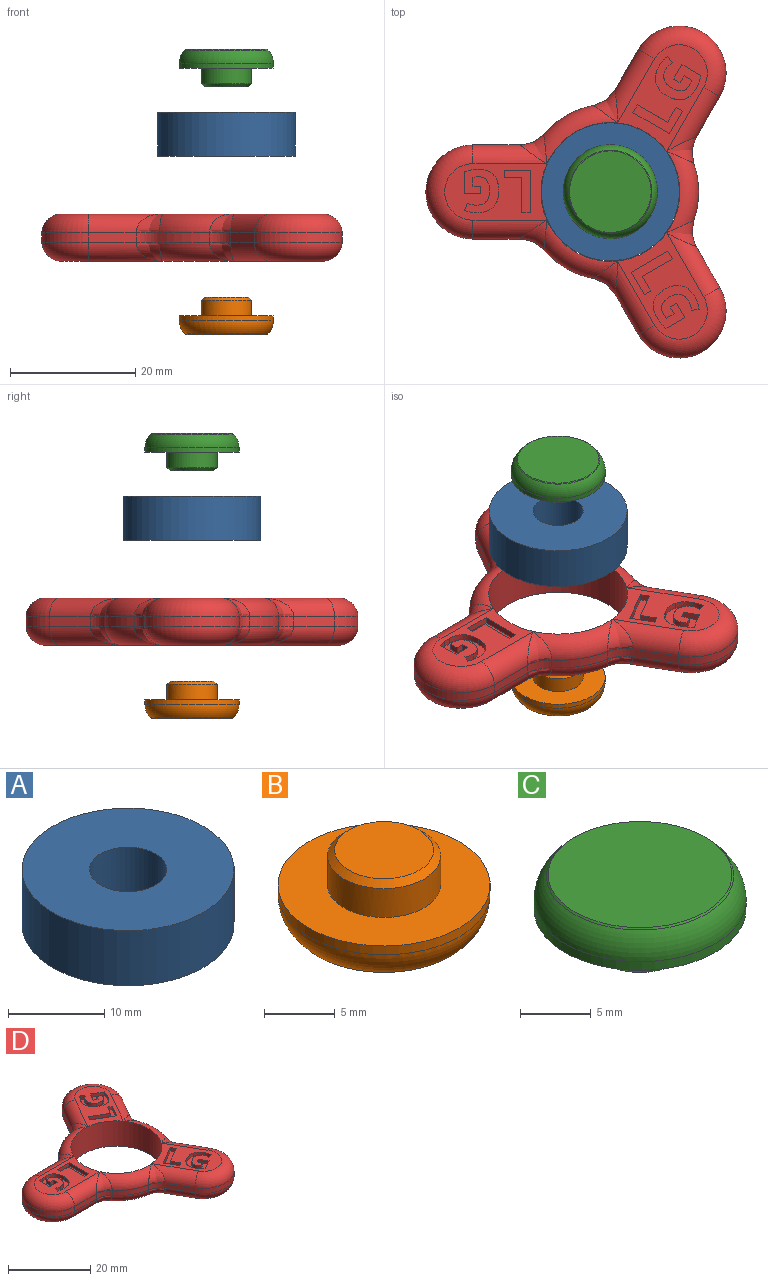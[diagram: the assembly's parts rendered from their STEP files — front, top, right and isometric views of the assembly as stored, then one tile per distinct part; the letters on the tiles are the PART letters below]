
ASSEMBLY  parts=4 mates=3
PART A: 4 faces, bbox 22x22x7 mm
  f0: cylinder r=4mm len=8mm, axis (0,0,-1), area 175.9mm2, adj f2,f3
  f1: cylinder r=11mm len=22mm, axis (0,0,-1), area 483.8mm2, adj f2,f3
  f2: plane 22x22mm, normal (0,0,1), area 329.9mm2, adj f0,f1
  f3: plane 22x22mm, normal (0,0,-1), area 329.9mm2, adj f0,f1
PART B: 8 faces, bbox 16.2x16.2x6.8 mm
  f0: cylinder r=4mm len=8mm, axis (0,0,-1), area 62.8mm2, adj f4,f7
  f1: plane 7x7mm, normal (0,0,1), area 38.5mm2, adj f7
  f2: cylinder r=7.5mm len=15mm, axis (0,0,1), area 35.7mm2, adj f4,f6
  f3: plane 13x13mm, normal (0,0,-1), area 132.7mm2, adj f5
  f4: plane 15x15mm, normal (0,0,1), area 126.4mm2, adj f0,f2
  f5: cone r=6.5mm half-angle=45deg, axis (0,0,1), area 7.1mm2, adj f3,f6
  f6: torus R=4.5mm, axis (0,0,-1), area 106.6mm2, adj f2,f5
  f7: cone r=3.5mm half-angle=45deg, axis (0,0,-1), area 16.7mm2, adj f0,f1
PART C: 8 faces, bbox 16.2x16.2x6.8 mm
  f0: cylinder r=4mm len=8mm, axis (0,0,1), area 62.8mm2, adj f4,f7
  f1: plane 7x7mm, normal (0,0,-1), area 38.5mm2, adj f7
  f2: cylinder r=7.5mm len=15mm, axis (0,0,-1), area 35.7mm2, adj f4,f6
  f3: plane 13x13mm, normal (0,0,1), area 132.7mm2, adj f5
  f4: plane 15x15mm, normal (0,0,-1), area 126.4mm2, adj f0,f2
  f5: cone r=6.5mm half-angle=45deg, axis (0,0,-1), area 7.1mm2, adj f3,f6
  f6: torus R=4.5mm, axis (0,0,1), area 106.6mm2, adj f2,f5
  f7: cone r=4mm half-angle=45deg, axis (0,0,1), area 16.7mm2, adj f0,f1
PART D: 223 faces, bbox 49.1x54.2x7.5 mm
  f0: plane 16.96x14.29mm, normal (0,0,1), area 97.3mm2, adj f9,f39,f41,f42,f196,f197,f198,f199
  f1: plane 16.96x14.29mm, normal (0,0,1), area 97.3mm2, adj f9,f31,f33,f35,f169,f170,f171,f172
  f2: plane 16.29x9mm, normal (0,0,1), area 97.3mm2, adj f9,f34,f36,f38,f142,f143,f144,f145
  f3: plane 16.96x14.29mm, normal (0,0,-1), area 97.3mm2, adj f9,f27,f29,f30,f115,f116,f117,f118
  f4: plane 16.96x14.29mm, normal (0,0,-1), area 97.3mm2, adj f9,f19,f21,f23,f88,f89,f90,f91
  f5: plane 16.29x9mm, normal (0,0,-1), area 97.3mm2, adj f9,f22,f24,f26,f61,f62,f63,f64
  f6: cylinder r=14.08mm len=9.19mm, axis (0,0,-1), area 14mm2, adj f25,f37,f47,f56
  f7: cylinder r=14.08mm len=7.96mm, axis (0,0,-1), area 14mm2, adj f20,f32,f44,f53
  f8: cylinder r=14.08mm len=7.96mm, axis (0,0,-1), area 14mm2, adj f28,f40,f50,f59
  f9: cylinder r=11.07mm len=22.15mm, axis (0,0,-1), area 521.9mm2, adj f0,f1,f2,f3,f4,f5,f20,f25
  f10: plane 7.5x1.5mm, normal (0,-1,0), area 11.3mm2, adj f12,f22,f34,f53
  f11: plane 7.5x1.5mm, normal (0,1,0), area 11.3mm2, adj f12,f26,f38,f50
  f12: cylinder r=7.5mm len=15mm, axis (0,0,-1), area 35.3mm2, adj f10,f11,f24,f36
  f13: plane 6.5x3.75mm, normal (0.87,0.5,0), area 11.3mm2, adj f15,f23,f35,f56
  f14: plane 6.5x3.75mm, normal (-0.87,-0.5,0), area 11.3mm2, adj f15,f19,f31,f44
  f15: cylinder r=7.5mm len=14mm, axis (0,0,-1), area 35.3mm2, adj f13,f14,f21,f33
  f16: plane 6.5x3.75mm, normal (-0.87,0.5,0), area 11.3mm2, adj f18,f30,f42,f59
  f17: plane 6.5x3.75mm, normal (0.87,-0.5,0), area 11.3mm2, adj f18,f27,f39,f47
  f18: cylinder r=7.5mm len=14mm, axis (0,0,-1), area 35.3mm2, adj f16,f17,f29,f41
  f19: cylinder r=3mm len=11.71mm, axis (0.5,-0.87,0), area 42.2mm2, adj f4,f14,f21,f43
  f20: torus R=11.07mm, axis (0,0,1), area 51mm2, adj f7,f9,f43,f52
  f21: torus R=4.5mm, axis (0,0,1), area 94.9mm2, adj f4,f15,f19,f23
  f22: cylinder r=3mm len=11.79mm, axis (1,0,0), area 42.2mm2, adj f5,f10,f24,f52
  f23: cylinder r=3mm len=11.71mm, axis (-0.5,0.87,0), area 42.2mm2, adj f4,f13,f21,f55
  f24: torus R=4.5mm, axis (0,0,1), area 94.9mm2, adj f5,f12,f22,f26
  f25: torus R=11.07mm, axis (0,0,1), area 51mm2, adj f6,f9,f46,f55
  f26: cylinder r=3mm len=11.79mm, axis (-1,0,0), area 42.2mm2, adj f5,f11,f24,f49
  f27: cylinder r=3mm len=11.71mm, axis (0.5,0.87,0), area 42.2mm2, adj f3,f17,f29,f46
  f28: torus R=11.07mm, axis (0,0,1), area 51mm2, adj f8,f9,f49,f58
  f29: torus R=4.5mm, axis (0,0,1), area 94.9mm2, adj f3,f18,f27,f30
  f30: cylinder r=3mm len=11.71mm, axis (-0.5,-0.87,0), area 42.2mm2, adj f3,f16,f29,f58
  f31: cylinder r=3mm len=11.71mm, axis (-0.5,0.87,0), area 42.2mm2, adj f1,f14,f33,f45
  f32: torus R=11.07mm, axis (0,0,1), area 51mm2, adj f7,f9,f45,f54
  f33: torus R=4.5mm, axis (0,0,1), area 94.9mm2, adj f1,f15,f31,f35
  f34: cylinder r=3mm len=11.79mm, axis (-1,0,0), area 42.2mm2, adj f2,f10,f36,f54
  f35: cylinder r=3mm len=11.71mm, axis (0.5,-0.87,0), area 42.2mm2, adj f1,f13,f33,f57
  f36: torus R=4.5mm, axis (0,0,1), area 94.9mm2, adj f2,f12,f34,f38
  f37: torus R=11.07mm, axis (0,0,1), area 51mm2, adj f6,f9,f48,f57
  f38: cylinder r=3mm len=11.79mm, axis (1,0,0), area 42.2mm2, adj f2,f11,f36,f51
  f39: cylinder r=3mm len=11.71mm, axis (-0.5,-0.87,0), area 42.2mm2, adj f0,f17,f41,f48
  f40: torus R=11.07mm, axis (0,0,1), area 51mm2, adj f8,f9,f51,f60
  f41: torus R=4.5mm, axis (0,0,1), area 94.9mm2, adj f0,f18,f39,f42
  f42: cylinder r=3mm len=11.71mm, axis (0.5,0.87,0), area 42.2mm2, adj f0,f16,f41,f60
  f43: bspline ~5.22x3.84mm, area 14.7mm2, adj f19,f20,f44
  f44: cylinder r=5mm len=3.38mm, axis (0,0,-1), area 6.4mm2, adj f7,f14,f43,f45
  f45: bspline ~5.22x3.84mm, area 14.7mm2, adj f31,f32,f44
  f46: bspline ~4.75x4.14mm, area 14.7mm2, adj f25,f27,f47
  f47: cylinder r=5mm len=4.13mm, axis (0,0,-1), area 6.4mm2, adj f6,f17,f46,f48
  f48: bspline ~4.75x4.14mm, area 14.7mm2, adj f37,f39,f47
  f49: bspline ~4.73x4.29mm, area 14.7mm2, adj f26,f28,f50
  f50: cylinder r=5mm len=3.78mm, axis (0,0,-1), area 6.4mm2, adj f8,f11,f49,f51
  f51: bspline ~4.73x4.29mm, area 14.7mm2, adj f38,f40,f50
  f52: bspline ~4.73x4.29mm, area 14.7mm2, adj f20,f22,f53
  f53: cylinder r=5mm len=3.78mm, axis (0,0,-1), area 6.4mm2, adj f7,f10,f52,f54
  f54: bspline ~4.73x4.29mm, area 14.7mm2, adj f32,f34,f53
  f55: bspline ~4.75x4.14mm, area 14.7mm2, adj f23,f25,f56
  f56: cylinder r=5mm len=4.13mm, axis (0,0,-1), area 6.4mm2, adj f6,f13,f55,f57
  f57: bspline ~4.75x4.14mm, area 14.7mm2, adj f35,f37,f56
  f58: bspline ~5.22x3.84mm, area 14.7mm2, adj f28,f30,f59
  f59: cylinder r=5mm len=3.38mm, axis (0,0,-1), area 6.4mm2, adj f8,f16,f58,f60
  f60: bspline ~5.22x3.84mm, area 14.7mm2, adj f40,f42,f59
  f61: plane 4.15x1mm, normal (0,1,0), area 4.2mm2, adj f5,f62,f66,f67
  f62: plane 1.18x1mm, normal (1,0,0), area 1.2mm2, adj f5,f61,f63,f67
  f63: plane 2.73x1mm, normal (0,-1,0), area 2.7mm2, adj f5,f62,f64,f67
  f64: plane 5.55x1mm, normal (1,0,0), area 5.5mm2, adj f5,f63,f65,f67
  f65: plane 1.43x1mm, normal (0,-1,0), area 1.4mm2, adj f5,f64,f66,f67
  f66: plane 6.73x1mm, normal (-1,0,0), area 6.7mm2, adj f5,f61,f65,f67
  f67: plane 6.73x4.15mm, normal (0,0,-1), area 12.8mm2, adj f61,f62,f63,f64,f65,f66
  f68: plane 1.19x1mm, normal (-1,0,0), area 1.2mm2, adj f5,f69,f86,f87
  f69: plane 1.27x1mm, normal (0,1,0), area 1.3mm2, adj f5,f68,f70,f87
  f70: plane 1.4x1mm, normal (-1,0,0), area 1.4mm2, adj f5,f69,f71,f87
  f71: extruded ~1x0.91mm, area 0.9mm2, adj f5,f70,f72,f87
  f72: extruded ~1.3x1mm, area 1.5mm2, adj f5,f71,f73,f87
  f73: extruded ~1.67x1mm, area 1.8mm2, adj f5,f72,f74,f87
  f74: extruded ~1.67x1mm, area 1.8mm2, adj f5,f73,f75,f87
  f75: extruded ~1.48x1mm, area 1.7mm2, adj f5,f74,f76,f87
  f76: extruded ~1.53x1mm, area 1.6mm2, adj f5,f75,f77,f87
  f77: plane 1.14x1mm, normal (0.92,0.38,0), area 1.2mm2, adj f5,f76,f78,f87
  f78: extruded ~2x1mm, area 2.1mm2, adj f5,f77,f79,f87
  f79: extruded ~2.58x1mm, area 2.8mm2, adj f5,f78,f80,f87
  f80: extruded ~2.54x1mm, area 2.8mm2, adj f5,f79,f81,f87
  f81: extruded ~2.57x1mm, area 2.8mm2, adj f5,f80,f82,f87
  f82: extruded ~2.32x1mm, area 2.6mm2, adj f5,f81,f83,f87
  f83: extruded ~1.17x1mm, area 1.2mm2, adj f5,f82,f84,f87
  f84: extruded ~1.22x1mm, area 1.3mm2, adj f5,f83,f85,f87
  f85: plane 3.49x1mm, normal (1,0,0), area 3.5mm2, adj f5,f84,f86,f87
  f86: plane 2.67x1mm, normal (0,-1,0), area 2.7mm2, adj f5,f68,f85,f87
  f87: plane 6.91x5.52mm, normal (0,0,-1), area 22mm2, adj f68,f69,f70,f71,f72,f73,f74,f75
  f88: plane 3.6x2.08mm, normal (-0.87,-0.5,0), area 4.2mm2, adj f4,f89,f93,f94
  f89: plane 1.02x1mm, normal (-0.5,0.87,0), area 1.2mm2, adj f4,f88,f90,f94
  f90: plane 2.36x1.36mm, normal (0.87,0.5,0), area 2.7mm2, adj f4,f89,f91,f94
  f91: plane 4.8x2.77mm, normal (-0.5,0.87,0), area 5.5mm2, adj f4,f90,f92,f94
  f92: plane 1.24x1mm, normal (0.87,0.5,0), area 1.4mm2, adj f4,f91,f93,f94
  f93: plane 5.82x3.36mm, normal (0.5,-0.87,0), area 6.7mm2, adj f4,f88,f92,f94
  f94: plane 7.9x4.6mm, normal (0,0,-1), area 12.8mm2, adj f88,f89,f90,f91,f92,f93
  f95: plane 1.03x1mm, normal (0.5,-0.87,0), area 1.2mm2, adj f4,f96,f113,f114
  f96: plane 1.1x1mm, normal (-0.87,-0.5,0), area 1.3mm2, adj f4,f95,f97,f114
  f97: plane 1.21x1mm, normal (0.5,-0.87,0), area 1.4mm2, adj f4,f96,f98,f114
  f98: extruded ~1x0.83mm, area 0.9mm2, adj f4,f97,f99,f114
  f99: extruded ~1.15x1mm, area 1.5mm2, adj f4,f98,f100,f114
  f100: extruded ~1.67x1mm, area 1.8mm2, adj f4,f99,f101,f114
  f101: extruded ~1.32x1.17mm, area 1.8mm2, adj f4,f100,f102,f114
  f102: extruded ~1.59x1mm, area 1.7mm2, adj f4,f101,f103,f114
  f103: extruded ~1.14x1.08mm, area 1.6mm2, adj f4,f102,f104,f114
  f104: plane 1x0.98mm, normal (-0.79,0.61,0), area 1.2mm2, adj f4,f103,f105,f114
  f105: extruded ~1.52x1.36mm, area 2.1mm2, adj f4,f104,f106,f114
  f106: extruded ~2.69x1mm, area 2.8mm2, adj f4,f105,f107,f114
  f107: extruded ~2.08x1.73mm, area 2.8mm2, adj f4,f106,f108,f114
  f108: extruded ~2.63x1mm, area 2.8mm2, adj f4,f107,f109,f114
  f109: extruded ~1.94x1.57mm, area 2.6mm2, adj f4,f108,f110,f114
  f110: extruded ~1.06x1mm, area 1.2mm2, adj f4,f109,f111,f114
  f111: extruded ~1.21x1mm, area 1.3mm2, adj f4,f110,f112,f114
  f112: plane 3.02x1.74mm, normal (-0.5,0.87,0), area 3.5mm2, adj f4,f111,f113,f114
  f113: plane 2.31x1.33mm, normal (0.87,0.5,0), area 2.7mm2, adj f4,f95,f112,f114
  f114: plane 7.36x7.04mm, normal (0,0,-1), area 22mm2, adj f95,f96,f97,f98,f99,f100,f101,f102
  f115: plane 1.03x1mm, normal (0.5,0.87,0), area 1.2mm2, adj f3,f116,f133,f134
  f116: plane 1.1x1mm, normal (0.87,-0.5,0), area 1.3mm2, adj f3,f115,f117,f134
  f117: plane 1.21x1mm, normal (0.5,0.87,0), area 1.4mm2, adj f3,f116,f118,f134
  f118: extruded ~1x0.74mm, area 0.9mm2, adj f3,f117,f119,f134
  f119: extruded ~1.42x1mm, area 1.5mm2, adj f3,f118,f120,f134
  f120: extruded ~1.22x1.22mm, area 1.8mm2, adj f3,f119,f121,f134
  f121: extruded ~1.72x1mm, area 1.8mm2, adj f3,f120,f122,f134
  f122: extruded ~1.28x1mm, area 1.7mm2, adj f3,f121,f123,f134
  f123: extruded ~1.51x1mm, area 1.6mm2, adj f3,f122,f124,f134
  f124: plane 1.23x1mm, normal (-0.13,-0.99,0), area 1.2mm2, adj f3,f123,f125,f134
  f125: extruded ~1.94x1mm, area 2.1mm2, adj f3,f124,f126,f134
  f126: extruded ~2.08x1.78mm, area 2.8mm2, adj f3,f125,f127,f134
  f127: extruded ~2.66x1mm, area 2.8mm2, adj f3,f126,f128,f134
  f128: extruded ~1.98x1.82mm, area 2.8mm2, adj f3,f127,f129,f134
  f129: extruded ~2.46x1mm, area 2.6mm2, adj f3,f128,f130,f134
  f130: extruded ~1x0.97mm, area 1.2mm2, adj f3,f129,f131,f134
  f131: extruded ~1x0.91mm, area 1.3mm2, adj f3,f130,f132,f134
  f132: plane 3.02x1.74mm, normal (-0.5,-0.87,0), area 3.5mm2, adj f3,f131,f133,f134
  f133: plane 2.31x1.33mm, normal (-0.87,0.5,0), area 2.7mm2, adj f3,f115,f132,f134
  f134: plane 7.43x7mm, normal (0,0,-1), area 22mm2, adj f115,f116,f117,f118,f119,f120,f121,f122
  f135: plane 3.6x2.08mm, normal (0.87,-0.5,0), area 4.2mm2, adj f3,f136,f140,f141
  f136: plane 1.02x1mm, normal (-0.5,-0.87,0), area 1.2mm2, adj f3,f135,f137,f141
  f137: plane 2.36x1.36mm, normal (-0.87,0.5,0), area 2.7mm2, adj f3,f136,f138,f141
  f138: plane 4.8x2.77mm, normal (-0.5,-0.87,0), area 5.5mm2, adj f3,f137,f139,f141
  f139: plane 1.24x1mm, normal (-0.87,0.5,0), area 1.4mm2, adj f3,f138,f140,f141
  f140: plane 5.82x3.36mm, normal (0.5,0.87,0), area 6.7mm2, adj f3,f135,f139,f141
  f141: plane 6.96x6.54mm, normal (0,0,-1), area 12.8mm2, adj f135,f136,f137,f138,f139,f140
  f142: plane 4.15x1mm, normal (0,-1,0), area 4.2mm2, adj f2,f143,f147,f148
  f143: plane 1.18x1mm, normal (1,0,0), area 1.2mm2, adj f2,f142,f144,f148
  f144: plane 2.73x1mm, normal (0,1,0), area 2.7mm2, adj f2,f143,f145,f148
  f145: plane 5.55x1mm, normal (1,0,0), area 5.5mm2, adj f2,f144,f146,f148
  f146: plane 1.43x1mm, normal (0,1,0), area 1.4mm2, adj f2,f145,f147,f148
  f147: plane 6.73x1mm, normal (-1,0,0), area 6.7mm2, adj f2,f142,f146,f148
  f148: plane 6.73x4.15mm, normal (0,0,1), area 12.8mm2, adj f142,f143,f144,f145,f146,f147
  f149: plane 1.19x1mm, normal (-1,0,0), area 1.2mm2, adj f2,f150,f167,f168
  f150: plane 1.27x1mm, normal (0,-1,0), area 1.3mm2, adj f2,f149,f151,f168
  f151: plane 1.4x1mm, normal (-1,0,0), area 1.4mm2, adj f2,f150,f152,f168
  f152: extruded ~1x0.91mm, area 0.9mm2, adj f2,f151,f153,f168
  f153: extruded ~1.3x1mm, area 1.5mm2, adj f2,f152,f154,f168
  f154: extruded ~1.67x1mm, area 1.8mm2, adj f2,f153,f155,f168
  f155: extruded ~1.67x1mm, area 1.8mm2, adj f2,f154,f156,f168
  f156: extruded ~1.48x1mm, area 1.7mm2, adj f2,f155,f157,f168
  f157: extruded ~1.53x1mm, area 1.6mm2, adj f2,f156,f158,f168
  f158: plane 1.14x1mm, normal (0.92,-0.38,0), area 1.2mm2, adj f2,f157,f159,f168
  f159: extruded ~2x1mm, area 2.1mm2, adj f2,f158,f160,f168
  f160: extruded ~2.58x1mm, area 2.8mm2, adj f2,f159,f161,f168
  f161: extruded ~2.54x1mm, area 2.8mm2, adj f2,f160,f162,f168
  f162: extruded ~2.57x1mm, area 2.8mm2, adj f2,f161,f163,f168
  f163: extruded ~2.32x1mm, area 2.6mm2, adj f2,f162,f164,f168
  f164: extruded ~1.17x1mm, area 1.2mm2, adj f2,f163,f165,f168
  f165: extruded ~1.22x1mm, area 1.3mm2, adj f2,f164,f166,f168
  f166: plane 3.49x1mm, normal (1,0,0), area 3.5mm2, adj f2,f165,f167,f168
  f167: plane 2.67x1mm, normal (0,1,0), area 2.7mm2, adj f2,f149,f166,f168
  f168: plane 6.91x5.52mm, normal (0,0,1), area 22mm2, adj f149,f150,f151,f152,f153,f154,f155,f156
  f169: plane 1.03x1mm, normal (0.5,-0.87,0), area 1.2mm2, adj f1,f170,f187,f188
  f170: plane 1.1x1mm, normal (0.87,0.5,0), area 1.3mm2, adj f1,f169,f171,f188
  f171: plane 1.21x1mm, normal (0.5,-0.87,0), area 1.4mm2, adj f1,f170,f172,f188
  f172: extruded ~1x0.74mm, area 0.9mm2, adj f1,f171,f173,f188
  f173: extruded ~1.42x1mm, area 1.5mm2, adj f1,f172,f174,f188
  f174: extruded ~1.22x1.22mm, area 1.8mm2, adj f1,f173,f175,f188
  f175: extruded ~1.72x1mm, area 1.8mm2, adj f1,f174,f176,f188
  f176: extruded ~1.28x1mm, area 1.7mm2, adj f1,f175,f177,f188
  f177: extruded ~1.51x1mm, area 1.6mm2, adj f1,f176,f178,f188
  f178: plane 1.23x1mm, normal (-0.13,0.99,0), area 1.2mm2, adj f1,f177,f179,f188
  f179: extruded ~1.94x1mm, area 2.1mm2, adj f1,f178,f180,f188
  f180: extruded ~2.08x1.78mm, area 2.8mm2, adj f1,f179,f181,f188
  f181: extruded ~2.66x1mm, area 2.8mm2, adj f1,f180,f182,f188
  f182: extruded ~1.98x1.82mm, area 2.8mm2, adj f1,f181,f183,f188
  f183: extruded ~2.46x1mm, area 2.6mm2, adj f1,f182,f184,f188
  f184: extruded ~1x0.97mm, area 1.2mm2, adj f1,f183,f185,f188
  f185: extruded ~1x0.91mm, area 1.3mm2, adj f1,f184,f186,f188
  f186: plane 3.02x1.74mm, normal (-0.5,0.87,0), area 3.5mm2, adj f1,f185,f187,f188
  f187: plane 2.31x1.33mm, normal (-0.87,-0.5,0), area 2.7mm2, adj f1,f169,f186,f188
  f188: plane 7.43x7mm, normal (0,0,1), area 22mm2, adj f169,f170,f171,f172,f173,f174,f175,f176
  f189: plane 3.6x2.08mm, normal (0.87,0.5,0), area 4.2mm2, adj f1,f190,f194,f195
  f190: plane 1.02x1mm, normal (-0.5,0.87,0), area 1.2mm2, adj f1,f189,f191,f195
  f191: plane 2.36x1.36mm, normal (-0.87,-0.5,0), area 2.7mm2, adj f1,f190,f192,f195
  f192: plane 4.8x2.77mm, normal (-0.5,0.87,0), area 5.5mm2, adj f1,f191,f193,f195
  f193: plane 1.24x1mm, normal (-0.87,-0.5,0), area 1.4mm2, adj f1,f192,f194,f195
  f194: plane 5.82x3.36mm, normal (0.5,-0.87,0), area 6.7mm2, adj f1,f189,f193,f195
  f195: plane 6.96x6.54mm, normal (0,0,1), area 12.8mm2, adj f189,f190,f191,f192,f193,f194
  f196: plane 3.6x2.08mm, normal (-0.87,0.5,0), area 4.2mm2, adj f0,f197,f201,f202
  f197: plane 1.02x1mm, normal (-0.5,-0.87,0), area 1.2mm2, adj f0,f196,f198,f202
  f198: plane 2.36x1.36mm, normal (0.87,-0.5,0), area 2.7mm2, adj f0,f197,f199,f202
  f199: plane 4.8x2.77mm, normal (-0.5,-0.87,0), area 5.5mm2, adj f0,f198,f200,f202
  f200: plane 1.24x1mm, normal (0.87,-0.5,0), area 1.4mm2, adj f0,f199,f201,f202
  f201: plane 5.82x3.36mm, normal (0.5,0.87,0), area 6.7mm2, adj f0,f196,f200,f202
  f202: plane 7.9x4.6mm, normal (0,0,1), area 12.8mm2, adj f196,f197,f198,f199,f200,f201
  f203: plane 1.03x1mm, normal (0.5,0.87,0), area 1.2mm2, adj f0,f204,f221,f222
  f204: plane 1.1x1mm, normal (-0.87,0.5,0), area 1.3mm2, adj f0,f203,f205,f222
  f205: plane 1.21x1mm, normal (0.5,0.87,0), area 1.4mm2, adj f0,f204,f206,f222
  f206: extruded ~1x0.83mm, area 0.9mm2, adj f0,f205,f207,f222
  f207: extruded ~1.15x1mm, area 1.5mm2, adj f0,f206,f208,f222
  f208: extruded ~1.67x1mm, area 1.8mm2, adj f0,f207,f209,f222
  f209: extruded ~1.32x1.17mm, area 1.8mm2, adj f0,f208,f210,f222
  f210: extruded ~1.59x1mm, area 1.7mm2, adj f0,f209,f211,f222
  f211: extruded ~1.14x1.08mm, area 1.6mm2, adj f0,f210,f212,f222
  f212: plane 1x0.98mm, normal (-0.79,-0.61,0), area 1.2mm2, adj f0,f211,f213,f222
  f213: extruded ~1.52x1.36mm, area 2.1mm2, adj f0,f212,f214,f222
  f214: extruded ~2.69x1mm, area 2.8mm2, adj f0,f213,f215,f222
  f215: extruded ~2.08x1.73mm, area 2.8mm2, adj f0,f214,f216,f222
  f216: extruded ~2.63x1mm, area 2.8mm2, adj f0,f215,f217,f222
  f217: extruded ~1.94x1.57mm, area 2.6mm2, adj f0,f216,f218,f222
  f218: extruded ~1.06x1mm, area 1.2mm2, adj f0,f217,f219,f222
  f219: extruded ~1.21x1mm, area 1.3mm2, adj f0,f218,f220,f222
  f220: plane 3.02x1.74mm, normal (-0.5,-0.87,0), area 3.5mm2, adj f0,f219,f221,f222
  f221: plane 2.31x1.33mm, normal (0.87,-0.5,0), area 2.7mm2, adj f0,f203,f220,f222
  f222: plane 7.36x7.04mm, normal (0,0,1), area 22mm2, adj f203,f204,f205,f206,f207,f208,f209,f210
PLACE A t=(-9.7,-3.31,20.9)mm
PLACE B t=(-9.7,-3.31,-4.56)mm
PLACE C t=(-9.7,-3.31,27.94)mm
PLACE D t=(-9.7,-3.31,4.42)mm fixed
MATE slider A.f0 <-> B.f0  axis (0,0,-1) through (-9.7,-3.31,24.65)mm
MATE slider A.f0 <-> D.f6  axis (0,0,-1) through (-9.7,-3.31,24.65)mm
MATE slider A.f0 <-> C.f0  axis (0,0,-1) through (-9.7,-3.31,24.65)mm
